# Revit family: EVISA
name_source: partatom
category: Equipement de génie climatique
revit_build: Autodesk Revit 2018 (Build: 20170223_1515(x64)
units: mm (PartAtom-declared; Revit-internal decimal feet)

## family parameters
Basée sur le plan de construction = Non
Classification = Aucun
Cote de connecteur circulaire = Utiliser le diamètre
Couper avec des vides une fois chargée = Non
Partagée = Non
Point de calcul de pièce = Non
Toujours verticalement = Oui
Type d'élément = Normal

## types (13) — shared parameters
BRANCHEMENT_TERRE = Oui
COS_PHI = 0.9
Fabricant = MIL'S
Lien espace client = https://www.mils.fr
Modèle = EVISA
NBR_POLES = 3
TENSION_ALIM = 400 V
ZONE_MAINT_200 = 200 mm
ZONE_MAINT_400 = 400 mm
ØBOUCH_OIL = 48.5 mm
ØVIDANGE = 30 mm  [stored 0.0984252 ft]

## per-type parameters (varying)
- i - E300.R: CHANF.CORPS=50 mm; CHANF.REF.V=40 mm  [stored 0.131234 ft]; CORPS=Oui; DEBIT_ASPI_VIDE=300.0 m³/h; DEBIT_REFOUL_VIDE=300.0 m³/h; DESCR_ALIM_ELECT=Alimentation électrique, 4G2.5mm²; DESCR_ASPI=Aspiration Vide ; 300 m³/h ; G 2" FEM; DESCR_REFOUL=Refoulement Vide ; 300 m³/h ; G 3" FEM; DIAM_ASPI_VIDE=50 mm; DIAM_REFOUL_VIDE=50 mm; HAUTEUR=426 mm; HAUT_BOITE_BORNE=362 mm; HAUT_BOITE_REFOUL.=420 mm; HAUT_BRIDE=360 mm; HAUT_CORPS=312.5 mm; HAUT_FILTRE_HUILE=82.5 mm; HAUT_MOT_ELECT.=170 mm; HAUT_OFFSET_VIDANGE=50 mm; HAUT_REFOUL.=477 mm; HAUT_REFOUL_E25/100.R=67.5 mm; HAUT_SILENTB.=31.5 mm  [stored 0.103346 ft]; LARGEUR=516 mm; LARG_BOITE_BORNE=125 mm; LARG_BOITE_REFOUL.=236 mm; LARG_CORPS=280 mm; LARG_ENTRAXE_SILENTB.=344.5 mm; LARG_OFFSET_BOITE_BORNE=62.5 mm; LARG_OFFSET_BRIDE=141 mm; LARG_OFFSET_CORPS=121 mm; LARG_OFFSET_COUDE_REFOUL.=277 mm; LARG_OFFSET_FILTRE=118 mm; LARG_OFFSET_MOT_ELECT.=35 mm  [stored 0.114829 ft]; LARG_OFFSET_OIL=53 mm; LARG_OFFSET_SILENTB_E25/100.R=235.7 mm; LARG_OFFSET_VIDANGE=192.5 mm; LARG_REFOUL_E25/100.R=62.2 mm; LONGUEUR=1063 mm; LONG_BOITE_BORNE=125 mm; LONG_BOITE_REFOUL.=610 mm; LONG_CORPS=688 mm; LONG_ENTRAXE_SILENTB.=260 mm; LONG_FILTRE_HUILE=138 mm; LONG_MOT_ELECT.=385.5 mm; LONG_OFFSET_BOITE_BORNE=8 mm  [stored 0.0262467 ft]; LONG_OFFSET_BRIDE=306.5 mm; LONG_OFFSET_CORPS=662.5 mm; LONG_OFFSET_REFOUL=440.5 mm; LONG_OFFSET_SILENTB_E25/100.R=104.6 mm; LONG_REFOUL.=61 mm; LONG_ZONE_MAINT=1463 mm; NEUTRE=Non; NIVEAU_SONORE(dB(A))=72; OFFSET_BOITE_REFOUL.=108.5 mm; POIDS(Kg)=172 mm; PROF.VIDANGE=36 mm  [stored 0.11811 ft]; PUISSANCE_APPARENTE=6111 VA; PUISS_ELECT=6 kW; RAY_COUDE_REFOUL.=48 mm; REFOUL_E40-100.R+SILENTB_N°5=Non; SILENTB_N°1=Oui; SILENTB_N°2=Oui; VISIBILITE_BRIDE=Non; ZONE_MAINT_50=161 mm; ØBRIDE=80 mm; ØCOUDE_REFOUL.=60 mm; ØFILTRE_HUILE=100 mm; ØMOT_ELECT.=264 mm; ØSILENTB.=50 mm
- a - E25.2 HV: CHANF.CORPS=36 mm  [stored 0.11811 ft]; CHANF.REF.V=5 mm  [stored 0.0164042 ft]; CORPS=Oui; DEBIT_ASPI_VIDE=30.0 m³/h; DEBIT_REFOUL_VIDE=30.0 m³/h; DESCR_ALIM_ELECT=Alimentation électrique, 4G1.5mm²; DESCR_ASPI=Aspiration Vide ; 30 m³/h ; G 1" FEM; DESCR_REFOUL=Refoulement Vide ; 30 m³/h ; G 1" FEM; DIAM_ASPI_VIDE=25 mm  [stored 0.082021 ft]; DIAM_REFOUL_VIDE=25 mm  [stored 0.082021 ft]; HAUTEUR=276 mm; HAUT_BOITE_BORNE=223 mm; HAUT_BOITE_REFOUL.=265 mm; HAUT_BRIDE=249.5 mm; HAUT_CORPS=209 mm; HAUT_FILTRE_HUILE=59 mm; HAUT_MOT_ELECT.=115.5 mm; HAUT_OFFSET_VIDANGE=29.5 mm; HAUT_REFOUL.=290 mm; HAUT_REFOUL_E25/100.R=67.5 mm; HAUT_SILENTB.=14 mm  [stored 0.0459318 ft]; LARGEUR=296 mm; LARG_BOITE_BORNE=94 mm; LARG_BOITE_REFOUL.=131 mm; LARG_CORPS=165 mm; LARG_ENTRAXE_SILENTB.=189 mm; LARG_OFFSET_BOITE_BORNE=47 mm; LARG_OFFSET_BRIDE=85 mm; LARG_OFFSET_CORPS=92 mm; LARG_OFFSET_COUDE_REFOUL.=144 mm; LARG_OFFSET_FILTRE=75 mm; LARG_OFFSET_MOT_ELECT.=0 mm  [stored 0 ft]; LARG_OFFSET_OIL=44 mm; LARG_OFFSET_SILENTB_E25/100.R=235.7 mm; LARG_OFFSET_VIDANGE=36.5 mm  [stored 0.119751 ft]; LARG_REFOUL_E25/100.R=62.2 mm; LONGUEUR=535 mm; LONG_BOITE_BORNE=94 mm; LONG_BOITE_REFOUL.=370 mm; LONG_CORPS=250 mm; LONG_ENTRAXE_SILENTB.=148 mm; LONG_FILTRE_HUILE=75 mm; LONG_MOT_ELECT.=251 mm; LONG_OFFSET_BOITE_BORNE=37 mm  [stored 0.121391 ft]; LONG_OFFSET_BRIDE=148 mm; LONG_OFFSET_CORPS=235 mm; LONG_OFFSET_REFOUL=174 mm; LONG_OFFSET_SILENTB_E25/100.R=104.6 mm; LONG_REFOUL.=42 mm  [stored 0.137795 ft]; LONG_ZONE_MAINT=935 mm; NEUTRE=Non; NIVEAU_SONORE(dB(A))=60; OFFSET_BOITE_REFOUL.=146 mm; POIDS(Kg)=39 mm  [stored 0.127953 ft]; PROF.VIDANGE=36 mm  [stored 0.11811 ft]; PUISSANCE_APPARENTE=833 VA; PUISS_ELECT=1 kW; RAY_COUDE_REFOUL.=31.2 mm  [stored 0.102362 ft]; REFOUL_E40-100.R+SILENTB_N°5=Non; SILENTB_N°1=Oui; SILENTB_N°2=Oui; VISIBILITE_BRIDE=Non; ZONE_MAINT_50=142 mm; ØBRIDE=50 mm; ØCOUDE_REFOUL.=39 mm  [stored 0.127953 ft]; ØFILTRE_HUILE=76 mm; ØMOT_ELECT.=156 mm; ØSILENTB.=30 mm  [stored 0.0984252 ft]
- j - E350.R: CHANF.CORPS=55 mm; CHANF.REF.V=12 mm  [stored 0.0393701 ft]; CORPS=Oui; DEBIT_ASPI_VIDE=360.0 m³/h; DEBIT_REFOUL_VIDE=360.0 m³/h; DESCR_ALIM_ELECT=Alimentation électrique, 4G4mm²; DESCR_ASPI=Aspiration Vide ; 360 m³/h ; BRIDE DN80; DESCR_REFOUL=Refoulement Vide ; 360 m³/h ; G 3" FEM; DIAM_ASPI_VIDE=80 mm; DIAM_REFOUL_VIDE=80 mm; HAUTEUR=544 mm; HAUT_BOITE_BORNE=443 mm; HAUT_BOITE_REFOUL.=533 mm; HAUT_BRIDE=509 mm; HAUT_CORPS=431 mm; HAUT_FILTRE_HUILE=95 mm; HAUT_MOT_ELECT.=210 mm; HAUT_OFFSET_VIDANGE=46 mm; HAUT_REFOUL.=614 mm; HAUT_REFOUL_E25/100.R=67.5 mm; HAUT_SILENTB.=28 mm  [stored 0.0918635 ft]; LARGEUR=682 mm; LARG_BOITE_BORNE=153 mm; LARG_BOITE_REFOUL.=299 mm; LARG_CORPS=383 mm; LARG_ENTRAXE_SILENTB.=464 mm; LARG_OFFSET_BOITE_BORNE=76.5 mm; LARG_OFFSET_BRIDE=170 mm; LARG_OFFSET_CORPS=188 mm; LARG_OFFSET_COUDE_REFOUL.=349 mm; LARG_OFFSET_FILTRE=220 mm; LARG_OFFSET_MOT_ELECT.=0 mm  [stored 0 ft]; LARG_OFFSET_OIL=51 mm; LARG_OFFSET_SILENTB_E25/100.R=235.7 mm; LARG_OFFSET_VIDANGE=235 mm; LARG_REFOUL_E25/100.R=62.2 mm; LONGUEUR=1360 mm; LONG_BOITE_BORNE=135 mm; LONG_BOITE_REFOUL.=686 mm; LONG_CORPS=837 mm; LONG_ENTRAXE_SILENTB.=376 mm; LONG_FILTRE_HUILE=121 mm; LONG_MOT_ELECT.=510 mm; LONG_OFFSET_BOITE_BORNE=43 mm  [stored 0.141076 ft]; LONG_OFFSET_BRIDE=349 mm; LONG_OFFSET_CORPS=758 mm; LONG_OFFSET_REFOUL=524 mm; LONG_OFFSET_SILENTB_E25/100.R=104.6 mm; LONG_REFOUL.=78 mm; LONG_ZONE_MAINT=1760 mm; NEUTRE=Non; NIVEAU_SONORE(dB(A))=72; OFFSET_BOITE_REFOUL.=82 mm; POIDS(Kg)=363 mm; PROF.VIDANGE=37 mm  [stored 0.121391 ft]; PUISSANCE_APPARENTE=8333 VA; PUISS_ELECT=8 kW; RAY_COUDE_REFOUL.=76 mm; REFOUL_E40-100.R+SILENTB_N°5=Non; SILENTB_N°1=Oui; SILENTB_N°2=Oui; VISIBILITE_BRIDE=Oui; ZONE_MAINT_50=178 mm; ØBRIDE=138 mm; ØCOUDE_REFOUL.=95 mm; ØFILTRE_HUILE=93 mm; ØMOT_ELECT.=310 mm; ØSILENTB.=60 mm
- c - E40.2 HV: CHANF.CORPS=36 mm  [stored 0.11811 ft]; CHANF.REF.V=5 mm  [stored 0.0164042 ft]; CORPS=Oui; DEBIT_ASPI_VIDE=47.7 m³/h; DEBIT_REFOUL_VIDE=47.7 m³/h; DESCR_ALIM_ELECT=Alimentation électrique, 4G1.5mm²; DESCR_ASPI=Aspiration Vide ; 47.7 m³/h ; G 1" FEM; DESCR_REFOUL=Refoulement Vide ; 47.7 m³/h ; G 1" FEM; DIAM_ASPI_VIDE=25 mm  [stored 0.082021 ft]; DIAM_REFOUL_VIDE=25 mm  [stored 0.082021 ft]; HAUTEUR=276 mm; HAUT_BOITE_BORNE=237.5 mm; HAUT_BOITE_REFOUL.=265 mm; HAUT_BRIDE=249.5 mm; HAUT_CORPS=209 mm; HAUT_FILTRE_HUILE=59 mm; HAUT_MOT_ELECT.=111.5 mm; HAUT_OFFSET_VIDANGE=29.5 mm; HAUT_REFOUL.=290 mm; HAUT_REFOUL_E25/100.R=67.5 mm; HAUT_SILENTB.=5 mm  [stored 0.0164042 ft]; LARGEUR=296 mm; LARG_BOITE_BORNE=109.5 mm; LARG_BOITE_REFOUL.=131 mm; LARG_CORPS=165 mm; LARG_ENTRAXE_SILENTB.=189 mm; LARG_OFFSET_BOITE_BORNE=54.8 mm; LARG_OFFSET_BRIDE=85 mm; LARG_OFFSET_CORPS=92 mm; LARG_OFFSET_COUDE_REFOUL.=144 mm; LARG_OFFSET_FILTRE=75 mm; LARG_OFFSET_MOT_ELECT.=0 mm  [stored 0 ft]; LARG_OFFSET_OIL=44 mm; LARG_OFFSET_SILENTB_E25/100.R=235.7 mm; LARG_OFFSET_VIDANGE=36.5 mm  [stored 0.119751 ft]; LARG_REFOUL_E25/100.R=62.2 mm; LONGUEUR=620 mm; LONG_BOITE_BORNE=109.5 mm; LONG_BOITE_REFOUL.=370 mm; LONG_CORPS=345 mm; LONG_ENTRAXE_SILENTB.=185 mm; LONG_FILTRE_HUILE=75 mm; LONG_MOT_ELECT.=274.5 mm; LONG_OFFSET_BOITE_BORNE=27.8 mm  [stored 0.0912073 ft]; LONG_OFFSET_BRIDE=185 mm; LONG_OFFSET_CORPS=337 mm; LONG_OFFSET_REFOUL=211 mm; LONG_OFFSET_SILENTB_E25/100.R=104.6 mm; LONG_REFOUL.=42 mm  [stored 0.137795 ft]; LONG_ZONE_MAINT=1020 mm; NEUTRE=Non; NIVEAU_SONORE(dB(A))=62; OFFSET_BOITE_REFOUL.=109 mm; POIDS(Kg)=52 mm; PROF.VIDANGE=36 mm  [stored 0.11811 ft]; PUISSANCE_APPARENTE=1222 VA; PUISS_ELECT=1 kW; RAY_COUDE_REFOUL.=25.6 mm; REFOUL_E40-100.R+SILENTB_N°5=Non; SILENTB_N°1=Oui; SILENTB_N°2=Oui; VISIBILITE_BRIDE=Non; ZONE_MAINT_50=142 mm; ØBRIDE=50 mm; ØCOUDE_REFOUL.=32 mm  [stored 0.104987 ft]; ØFILTRE_HUILE=76 mm; ØMOT_ELECT.=175 mm; ØSILENTB.=30 mm  [stored 0.0984252 ft]
- g - E150.R: CHANF.CORPS=40 mm  [stored 0.131234 ft]; CHANF.REF.V=40 mm  [stored 0.131234 ft]; CORPS=Oui; DEBIT_ASPI_VIDE=132.0 m³/h; DEBIT_REFOUL_VIDE=132.0 m³/h; DESCR_ALIM_ELECT=Alimentation électrique, 4G2.5mm²; DESCR_ASPI=Aspiration Vide ; 132 m³/h ; G 2" FEM; DESCR_REFOUL=Refoulement Vide ; 132 m³/h ; G 2" FEM; DIAM_ASPI_VIDE=50 mm; DIAM_REFOUL_VIDE=50 mm; HAUTEUR=426 mm; HAUT_BOITE_BORNE=353 mm; HAUT_BOITE_REFOUL.=420 mm; HAUT_BRIDE=360 mm; HAUT_CORPS=312.5 mm; HAUT_FILTRE_HUILE=82.5 mm; HAUT_MOT_ELECT.=168 mm; HAUT_OFFSET_VIDANGE=50 mm; HAUT_REFOUL.=477 mm; HAUT_REFOUL_E25/100.R=67.5 mm; HAUT_SILENTB.=25 mm  [stored 0.082021 ft]; LARGEUR=516 mm; LARG_BOITE_BORNE=127 mm; LARG_BOITE_REFOUL.=238 mm; LARG_CORPS=278 mm; LARG_ENTRAXE_SILENTB.=344.5 mm; LARG_OFFSET_BOITE_BORNE=63.5 mm; LARG_OFFSET_BRIDE=141 mm; LARG_OFFSET_CORPS=121 mm; LARG_OFFSET_COUDE_REFOUL.=277 mm; LARG_OFFSET_FILTRE=118 mm; LARG_OFFSET_MOT_ELECT.=42.5 mm  [stored 0.139436 ft]; LARG_OFFSET_OIL=53 mm; LARG_OFFSET_SILENTB_E25/100.R=235.7 mm; LARG_OFFSET_VIDANGE=192.5 mm; LARG_REFOUL_E25/100.R=62.2 mm; LONGUEUR=919 mm; LONG_BOITE_BORNE=127 mm; LONG_BOITE_REFOUL.=610 mm; LONG_CORPS=504 mm; LONG_ENTRAXE_SILENTB.=260 mm; LONG_FILTRE_HUILE=138 mm; LONG_MOT_ELECT.=385.5 mm; LONG_OFFSET_BOITE_BORNE=33 mm  [stored 0.108268 ft]; LONG_OFFSET_BRIDE=260 mm; LONG_OFFSET_CORPS=478.5 mm; LONG_OFFSET_REFOUL=394 mm; LONG_OFFSET_SILENTB_E25/100.R=104.6 mm; LONG_REFOUL.=65 mm; LONG_ZONE_MAINT=1319 mm; NEUTRE=Non; NIVEAU_SONORE(dB(A))=69; OFFSET_BOITE_REFOUL.=155 mm; POIDS(Kg)=154 mm; PROF.VIDANGE=41 mm  [stored 0.134514 ft]; PUISSANCE_APPARENTE=3333 VA; PUISS_ELECT=3 kW; RAY_COUDE_REFOUL.=51.6 mm; REFOUL_E40-100.R+SILENTB_N°5=Non; SILENTB_N°1=Oui; SILENTB_N°2=Oui; VISIBILITE_BRIDE=Non; ZONE_MAINT_50=165 mm; ØBRIDE=80 mm; ØCOUDE_REFOUL.=64.5 mm; ØFILTRE_HUILE=93 mm; ØMOT_ELECT.=255 mm; ØSILENTB.=50 mm
- h - E200.R: CHANF.CORPS=40 mm  [stored 0.131234 ft]; CHANF.REF.V=40 mm  [stored 0.131234 ft]; CORPS=Oui; DEBIT_ASPI_VIDE=200.0 m³/h; DEBIT_REFOUL_VIDE=200.0 m³/h; DESCR_ALIM_ELECT=Alimentation électrique, 4G2.5mm²; DESCR_ASPI=Aspiration Vide ; 200 m³/h ; G 2" FEM; DESCR_REFOUL=Refoulement Vide ; 200 m³/h ; G 2" FEM; DIAM_ASPI_VIDE=50 mm; DIAM_REFOUL_VIDE=50 mm; HAUTEUR=426 mm; HAUT_BOITE_BORNE=320 mm; HAUT_BOITE_REFOUL.=420 mm; HAUT_BRIDE=360 mm; HAUT_CORPS=312.5 mm; HAUT_FILTRE_HUILE=82.5 mm; HAUT_MOT_ELECT.=172 mm; HAUT_OFFSET_VIDANGE=50 mm; HAUT_REFOUL.=477 mm; HAUT_REFOUL_E25/100.R=67.5 mm; HAUT_SILENTB.=25 mm  [stored 0.082021 ft]; LARGEUR=516 mm; LARG_BOITE_BORNE=86 mm; LARG_BOITE_REFOUL.=238 mm; LARG_CORPS=278 mm; LARG_ENTRAXE_SILENTB.=344.5 mm; LARG_OFFSET_BOITE_BORNE=43 mm  [stored 0.141076 ft]; LARG_OFFSET_BRIDE=141 mm; LARG_OFFSET_CORPS=121 mm; LARG_OFFSET_COUDE_REFOUL.=277 mm; LARG_OFFSET_FILTRE=118 mm; LARG_OFFSET_MOT_ELECT.=35 mm  [stored 0.114829 ft]; LARG_OFFSET_OIL=53 mm; LARG_OFFSET_SILENTB_E25/100.R=235.7 mm; LARG_OFFSET_VIDANGE=192.5 mm; LARG_REFOUL_E25/100.R=62.2 mm; LONGUEUR=917 mm; LONG_BOITE_BORNE=86 mm; LONG_BOITE_REFOUL.=610 mm; LONG_CORPS=594.5 mm; LONG_ENTRAXE_SILENTB.=260 mm; LONG_FILTRE_HUILE=138 mm; LONG_MOT_ELECT.=323 mm; LONG_OFFSET_BOITE_BORNE=31.7 mm  [stored 0.104003 ft]; LONG_OFFSET_BRIDE=260 mm; LONG_OFFSET_CORPS=569 mm; LONG_OFFSET_REFOUL=394 mm; LONG_OFFSET_SILENTB_E25/100.R=104.6 mm; LONG_REFOUL.=61 mm; LONG_ZONE_MAINT=1317 mm; NEUTRE=Non; NIVEAU_SONORE(dB(A))=71; OFFSET_BOITE_REFOUL.=155 mm; POIDS(Kg)=143 mm; PROF.VIDANGE=38 mm  [stored 0.124672 ft]; PUISSANCE_APPARENTE=4444 VA; PUISS_ELECT=4 kW; RAY_COUDE_REFOUL.=51.6 mm; REFOUL_E40-100.R+SILENTB_N°5=Non; SILENTB_N°1=Oui; SILENTB_N°2=Oui; VISIBILITE_BRIDE=Non; ZONE_MAINT_50=161 mm; ØBRIDE=80 mm; ØCOUDE_REFOUL.=64.5 mm; ØFILTRE_HUILE=93 mm; ØMOT_ELECT.=220 mm; ØSILENTB.=50 mm
- k - E400.R: CHANF.CORPS=55 mm; CHANF.REF.V=10 mm  [stored 0.0328084 ft]; CORPS=Oui; DEBIT_ASPI_VIDE=426.0 m³/h; DEBIT_REFOUL_VIDE=426.0 m³/h; DESCR_ALIM_ELECT=Alimentation électrique, 4G6mm²; DESCR_ASPI=Aspiration Vide ; 426 m³/h ; BRIDE DN80; DESCR_REFOUL=Refoulement Vide ; 426 m³/h ; G 3" FEM; DIAM_ASPI_VIDE=80 mm; DIAM_REFOUL_VIDE=80 mm; HAUTEUR=544 mm; HAUT_BOITE_BORNE=443 mm; HAUT_BOITE_REFOUL.=533 mm; HAUT_BRIDE=509 mm; HAUT_CORPS=431 mm; HAUT_FILTRE_HUILE=95 mm; HAUT_MOT_ELECT.=210 mm; HAUT_OFFSET_VIDANGE=46 mm; HAUT_REFOUL.=614 mm; HAUT_REFOUL_E25/100.R=67.5 mm; HAUT_SILENTB.=28 mm  [stored 0.0918635 ft]; LARGEUR=680 mm; LARG_BOITE_BORNE=153 mm; LARG_BOITE_REFOUL.=299 mm; LARG_CORPS=383 mm; LARG_ENTRAXE_SILENTB.=464 mm; LARG_OFFSET_BOITE_BORNE=76.5 mm; LARG_OFFSET_BRIDE=170 mm; LARG_OFFSET_CORPS=188 mm; LARG_OFFSET_COUDE_REFOUL.=349 mm; LARG_OFFSET_FILTRE=220 mm; LARG_OFFSET_MOT_ELECT.=0 mm  [stored 0 ft]; LARG_OFFSET_OIL=51 mm; LARG_OFFSET_SILENTB_E25/100.R=235.7 mm; LARG_OFFSET_VIDANGE=235 mm; LARG_REFOUL_E25/100.R=62.2 mm; LONGUEUR=1400 mm; LONG_BOITE_BORNE=135 mm; LONG_BOITE_REFOUL.=685.5 mm; LONG_CORPS=883.5 mm; LONG_ENTRAXE_SILENTB.=376 mm; LONG_FILTRE_HUILE=121 mm; LONG_MOT_ELECT.=510 mm; LONG_OFFSET_BOITE_BORNE=43 mm  [stored 0.141076 ft]; LONG_OFFSET_BRIDE=376 mm; LONG_OFFSET_CORPS=827.5 mm; LONG_OFFSET_REFOUL=523.5 mm; LONG_OFFSET_SILENTB_E25/100.R=104.6 mm; LONG_REFOUL.=78 mm; LONG_ZONE_MAINT=1800 mm; NEUTRE=Non; NIVEAU_SONORE(dB(A))=72; OFFSET_BOITE_REFOUL.=81.5 mm; POIDS(Kg)=408 mm; PROF.VIDANGE=27.5 mm  [stored 0.0902231 ft]; PUISSANCE_APPARENTE=10000 VA; PUISS_ELECT=9 kW; RAY_COUDE_REFOUL.=76 mm; REFOUL_E40-100.R+SILENTB_N°5=Non; SILENTB_N°1=Oui; SILENTB_N°2=Oui; VISIBILITE_BRIDE=Oui; ZONE_MAINT_50=178 mm; ØBRIDE=138 mm; ØCOUDE_REFOUL.=95 mm; ØFILTRE_HUILE=93 mm; ØMOT_ELECT.=310 mm; ØSILENTB.=60 mm
- l - E500.R: CHANF.CORPS=55 mm; CHANF.REF.V=12 mm  [stored 0.0393701 ft]; CORPS=Oui; DEBIT_ASPI_VIDE=513.0 m³/h; DEBIT_REFOUL_VIDE=513.0 m³/h; DESCR_ALIM_ELECT=Alimentation électrique, 4G6mm²; DESCR_ASPI=Aspiration Vide ; 513 m³/h ; BRIDE DN80; DESCR_REFOUL=Refoulement Vide ; 513 m³/h ; G 3" FEM; DIAM_ASPI_VIDE=80 mm; DIAM_REFOUL_VIDE=80 mm; HAUTEUR=544 mm; HAUT_BOITE_BORNE=466 mm; HAUT_BOITE_REFOUL.=533 mm; HAUT_BRIDE=509 mm; HAUT_CORPS=431 mm; HAUT_FILTRE_HUILE=95 mm; HAUT_MOT_ELECT.=210 mm; HAUT_OFFSET_VIDANGE=46 mm; HAUT_REFOUL.=614 mm; HAUT_REFOUL_E25/100.R=67.5 mm; HAUT_SILENTB.=28 mm  [stored 0.0918635 ft]; LARGEUR=680 mm; LARG_BOITE_BORNE=210 mm; LARG_BOITE_REFOUL.=299 mm; LARG_CORPS=381 mm; LARG_ENTRAXE_SILENTB.=464 mm; LARG_OFFSET_BOITE_BORNE=105 mm; LARG_OFFSET_BRIDE=168 mm; LARG_OFFSET_CORPS=186 mm; LARG_OFFSET_COUDE_REFOUL.=349 mm; LARG_OFFSET_FILTRE=220 mm; LARG_OFFSET_MOT_ELECT.=0 mm  [stored 0 ft]; LARG_OFFSET_OIL=51 mm; LARG_OFFSET_SILENTB_E25/100.R=235.7 mm; LARG_OFFSET_VIDANGE=235 mm; LARG_REFOUL_E25/100.R=62.2 mm; LONGUEUR=1500 mm; LONG_BOITE_BORNE=180 mm; LONG_BOITE_REFOUL.=685.5 mm; LONG_CORPS=943.5 mm; LONG_ENTRAXE_SILENTB.=376 mm; LONG_FILTRE_HUILE=121 mm; LONG_MOT_ELECT.=552 mm; LONG_OFFSET_BOITE_BORNE=67 mm; LONG_OFFSET_BRIDE=376 mm; LONG_OFFSET_CORPS=853.5 mm; LONG_OFFSET_REFOUL=523.5 mm; LONG_OFFSET_SILENTB_E25/100.R=104.6 mm; LONG_REFOUL.=78 mm; LONG_ZONE_MAINT=1900 mm; NEUTRE=Non; NIVEAU_SONORE(dB(A))=73; OFFSET_BOITE_REFOUL.=81.5 mm; POIDS(Kg)=462 mm; PROF.VIDANGE=27.5 mm  [stored 0.0902231 ft]; PUISSANCE_APPARENTE=12222 VA; PUISS_ELECT=11 kW; RAY_COUDE_REFOUL.=76 mm; REFOUL_E40-100.R+SILENTB_N°5=Non; SILENTB_N°1=Oui; SILENTB_N°2=Oui; VISIBILITE_BRIDE=Oui; ZONE_MAINT_50=178 mm; ØBRIDE=138 mm; ØCOUDE_REFOUL.=95 mm; ØFILTRE_HUILE=93 mm; ØMOT_ELECT.=348 mm; ØSILENTB.=60 mm
- m - E600.R: CHANF.CORPS=55 mm; CHANF.REF.V=12 mm  [stored 0.0393701 ft]; CORPS=Oui; DEBIT_ASPI_VIDE=635.0 m³/h; DEBIT_REFOUL_VIDE=635.0 m³/h; DESCR_ALIM_ELECT=Alimentation électrique 4G10mm²; DESCR_ASPI=Aspiration Vide ; 635 m³/h ; BRIDE DN80; DESCR_REFOUL=Refoulement Vide ; 635 m³/h ; G 3" FEM; DIAM_ASPI_VIDE=80 mm; DIAM_REFOUL_VIDE=80 mm; HAUTEUR=544 mm; HAUT_BOITE_BORNE=466 mm; HAUT_BOITE_REFOUL.=533 mm; HAUT_BRIDE=509 mm; HAUT_CORPS=431 mm; HAUT_FILTRE_HUILE=95 mm; HAUT_MOT_ELECT.=210 mm; HAUT_OFFSET_VIDANGE=46 mm; HAUT_REFOUL.=611 mm; HAUT_REFOUL_E25/100.R=67.5 mm; HAUT_SILENTB.=28 mm  [stored 0.0918635 ft]; LARGEUR=680 mm; LARG_BOITE_BORNE=210 mm; LARG_BOITE_REFOUL.=299 mm; LARG_CORPS=381 mm; LARG_ENTRAXE_SILENTB.=464 mm; LARG_OFFSET_BOITE_BORNE=105 mm; LARG_OFFSET_BRIDE=168 mm; LARG_OFFSET_CORPS=186 mm; LARG_OFFSET_COUDE_REFOUL.=349 mm; LARG_OFFSET_FILTRE=220 mm; LARG_OFFSET_MOT_ELECT.=0 mm  [stored 0 ft]; LARG_OFFSET_OIL=51 mm; LARG_OFFSET_SILENTB_E25/100.R=235.7 mm; LARG_OFFSET_VIDANGE=235 mm; LARG_REFOUL_E25/100.R=62.2 mm; LONGUEUR=1655 mm; LONG_BOITE_BORNE=180 mm; LONG_BOITE_REFOUL.=685.5 mm; LONG_CORPS=1035 mm; LONG_ENTRAXE_SILENTB.=376 mm; LONG_FILTRE_HUILE=121 mm; LONG_MOT_ELECT.=614 mm; LONG_OFFSET_BOITE_BORNE=65.5 mm; LONG_OFFSET_BRIDE=376 mm; LONG_OFFSET_CORPS=900 mm; LONG_OFFSET_REFOUL=523.5 mm; LONG_OFFSET_SILENTB_E25/100.R=104.6 mm; LONG_REFOUL.=78 mm; LONG_ZONE_MAINT=2055 mm; NEUTRE=Non; NIVEAU_SONORE(dB(A))=74; OFFSET_BOITE_REFOUL.=81.5 mm; POIDS(Kg)=531 mm; PROF.VIDANGE=27.5 mm  [stored 0.0902231 ft]; PUISSANCE_APPARENTE=14444 VA; PUISS_ELECT=13 kW; RAY_COUDE_REFOUL.=76 mm; REFOUL_E40-100.R+SILENTB_N°5=Non; SILENTB_N°1=Oui; SILENTB_N°2=Oui; VISIBILITE_BRIDE=Oui; ZONE_MAINT_50=178 mm; ØBRIDE=138 mm; ØCOUDE_REFOUL.=95 mm; ØFILTRE_HUILE=93 mm; ØMOT_ELECT.=348 mm; ØSILENTB.=60 mm
- b - E25.R: CHANF.CORPS=36 mm  [stored 0.11811 ft]; CHANF.REF.V=5 mm  [stored 0.0164042 ft]; CORPS=Non; DEBIT_ASPI_VIDE=28.0 m³/h; DEBIT_REFOUL_VIDE=28.0 m³/h; DESCR_ALIM_ELECT=Alimentation électrique, 4G1.5mm²; DESCR_ASPI=Aspiration Vide ; 28 m³/h ; G 1" FEM; DESCR_REFOUL=Refoulement Vide ; 28 m³/h ; G 1" FEM; DIAM_ASPI_VIDE=25 mm  [stored 0.082021 ft]; DIAM_REFOUL_VIDE=25 mm  [stored 0.082021 ft]; HAUTEUR=258 mm; HAUT_BOITE_BORNE=237 mm; HAUT_BOITE_REFOUL.=258 mm; HAUT_BRIDE=228 mm; HAUT_CORPS=180 mm; HAUT_FILTRE_HUILE=65.5 mm; HAUT_MOT_ELECT.=115.5 mm; HAUT_OFFSET_VIDANGE=38.5 mm  [stored 0.126312 ft]; HAUT_REFOUL.=225 mm; HAUT_REFOUL_E25/100.R=55 mm; HAUT_SILENTB.=21 mm  [stored 0.0688976 ft]; LARGEUR=300 mm; LARG_BOITE_BORNE=85 mm; LARG_BOITE_REFOUL.=128 mm; LARG_CORPS=172.2 mm; LARG_ENTRAXE_SILENTB.=253.5 mm; LARG_OFFSET_BOITE_BORNE=42.5 mm  [stored 0.139436 ft]; LARG_OFFSET_BRIDE=85 mm; LARG_OFFSET_CORPS=22.2 mm  [stored 0.0728346 ft]; LARG_OFFSET_COUDE_REFOUL.=131 mm; LARG_OFFSET_FILTRE=62 mm; LARG_OFFSET_MOT_ELECT.=72.3 mm; LARG_OFFSET_OIL=44 mm; LARG_OFFSET_SILENTB_E25/100.R=253.5 mm; LARG_OFFSET_VIDANGE=63.3 mm; LARG_REFOUL_E25/100.R=45 mm; LONGUEUR=443 mm; LONG_BOITE_BORNE=85 mm; LONG_BOITE_REFOUL.=312 mm; LONG_CORPS=49 mm; LONG_ENTRAXE_SILENTB.=187 mm; LONG_FILTRE_HUILE=76 mm; LONG_MOT_ELECT.=397.5 mm; LONG_OFFSET_BOITE_BORNE=179 mm; LONG_OFFSET_BRIDE=159 mm; LONG_OFFSET_CORPS=300 mm; LONG_OFFSET_REFOUL=214 mm; LONG_OFFSET_SILENTB_E25/100.R=104.6 mm; LONG_REFOUL.=31 mm; LONG_ZONE_MAINT=843 mm; NEUTRE=Oui; NIVEAU_SONORE(dB(A))=59; OFFSET_BOITE_REFOUL.=67 mm; POIDS(Kg)=30 mm  [stored 0.0984252 ft]; PROF.VIDANGE=37 mm  [stored 0.121391 ft]; PUISSANCE_APPARENTE=833 VA; PUISS_ELECT=1 kW; RAY_COUDE_REFOUL.=24 mm  [stored 0.0787402 ft]; REFOUL_E40-100.R+SILENTB_N°5=Oui; SILENTB_N°1=Non; SILENTB_N°2=Non; VISIBILITE_BRIDE=Non; ZONE_MAINT_50=131 mm; ØBRIDE=50 mm; ØCOUDE_REFOUL.=30 mm  [stored 0.0984252 ft]; ØFILTRE_HUILE=76 mm; ØMOT_ELECT.=189 mm; ØSILENTB.=30 mm  [stored 0.0984252 ft]
- d - E40.R: CHANF.CORPS=36 mm  [stored 0.11811 ft]; CHANF.REF.V=5 mm  [stored 0.0164042 ft]; CORPS=Non; DEBIT_ASPI_VIDE=44.0 m³/h; DEBIT_REFOUL_VIDE=44.0 m³/h; DESCR_ALIM_ELECT=Alimentation électrique, 4G1.5mm²; DESCR_ASPI=Aspiration Vide ; 44 m³/h ; G 1" FEM; DESCR_REFOUL=Refoulement Vide ; 44 m³/h ; G 1" FEM; DIAM_ASPI_VIDE=25 mm  [stored 0.082021 ft]; DIAM_REFOUL_VIDE=25 mm  [stored 0.082021 ft]; HAUTEUR=258 mm; HAUT_BOITE_BORNE=237 mm; HAUT_BOITE_REFOUL.=257 mm; HAUT_BRIDE=228 mm; HAUT_CORPS=180 mm; HAUT_FILTRE_HUILE=65.5 mm; HAUT_MOT_ELECT.=115.5 mm; HAUT_OFFSET_VIDANGE=38.5 mm  [stored 0.126312 ft]; HAUT_REFOUL.=225 mm; HAUT_REFOUL_E25/100.R=55 mm; HAUT_SILENTB.=21 mm  [stored 0.0688976 ft]; LARGEUR=300 mm; LARG_BOITE_BORNE=85 mm; LARG_BOITE_REFOUL.=128 mm; LARG_CORPS=172.2 mm; LARG_ENTRAXE_SILENTB.=253.5 mm; LARG_OFFSET_BOITE_BORNE=42.5 mm  [stored 0.139436 ft]; LARG_OFFSET_BRIDE=85 mm; LARG_OFFSET_CORPS=22.2 mm  [stored 0.0728346 ft]; LARG_OFFSET_COUDE_REFOUL.=131 mm; LARG_OFFSET_FILTRE=62 mm; LARG_OFFSET_MOT_ELECT.=72.3 mm; LARG_OFFSET_OIL=44 mm; LARG_OFFSET_SILENTB_E25/100.R=253.5 mm; LARG_OFFSET_VIDANGE=63.3 mm; LARG_REFOUL_E25/100.R=47.5 mm; LONGUEUR=443 mm; LONG_BOITE_BORNE=85 mm; LONG_BOITE_REFOUL.=312 mm; LONG_CORPS=49 mm; LONG_ENTRAXE_SILENTB.=187 mm; LONG_FILTRE_HUILE=76 mm; LONG_MOT_ELECT.=397.5 mm; LONG_OFFSET_BOITE_BORNE=179 mm; LONG_OFFSET_BRIDE=159 mm; LONG_OFFSET_CORPS=300 mm; LONG_OFFSET_REFOUL=214 mm; LONG_OFFSET_SILENTB_E25/100.R=104.6 mm; LONG_REFOUL.=31 mm; LONG_ZONE_MAINT=843 mm; NEUTRE=Non; NIVEAU_SONORE(dB(A))=58; OFFSET_BOITE_REFOUL.=67 mm; POIDS(Kg)=34.3 mm  [stored 0.112533 ft]; PROF.VIDANGE=37 mm  [stored 0.121391 ft]; PUISSANCE_APPARENTE=1222 VA; PUISS_ELECT=1 kW; RAY_COUDE_REFOUL.=24 mm  [stored 0.0787402 ft]; REFOUL_E40-100.R+SILENTB_N°5=Oui; SILENTB_N°1=Non; SILENTB_N°2=Non; VISIBILITE_BRIDE=Non; ZONE_MAINT_50=131 mm; ØBRIDE=50 mm; ØCOUDE_REFOUL.=30 mm  [stored 0.0984252 ft]; ØFILTRE_HUILE=76 mm; ØMOT_ELECT.=189 mm; ØSILENTB.=30 mm  [stored 0.0984252 ft]
- e - E65.R: CHANF.CORPS=36 mm  [stored 0.11811 ft]; CHANF.REF.V=25 mm  [stored 0.082021 ft]; CORPS=Non; DEBIT_ASPI_VIDE=68.0 m³/h; DEBIT_REFOUL_VIDE=68.0 m³/h; DESCR_ALIM_ELECT=Alimentation électrique, 4G1.5mm²; DESCR_ASPI=Aspiration Vide ; 68 m³/h ; G 1"1/4 FEM; DESCR_REFOUL=Refoulement Vide ; 68 m³/h ; G 1"1/4 FEM; DIAM_ASPI_VIDE=32 mm  [stored 0.104987 ft]; DIAM_REFOUL_VIDE=32 mm  [stored 0.104987 ft]; HAUTEUR=285 mm; HAUT_BOITE_BORNE=253 mm; HAUT_BOITE_REFOUL.=285 mm; HAUT_BRIDE=279 mm; HAUT_CORPS=180 mm; HAUT_FILTRE_HUILE=65.5 mm; HAUT_MOT_ELECT.=127 mm; HAUT_OFFSET_VIDANGE=43.5 mm  [stored 0.142717 ft]; HAUT_REFOUL.=248 mm; HAUT_REFOUL_E25/100.R=60 mm; HAUT_SILENTB.=23 mm  [stored 0.0754593 ft]; LARGEUR=331 mm; LARG_BOITE_BORNE=110 mm; LARG_BOITE_REFOUL.=127 mm; LARG_CORPS=204 mm; LARG_ENTRAXE_SILENTB.=205 mm; LARG_OFFSET_BOITE_BORNE=55 mm; LARG_OFFSET_BRIDE=107.5 mm; LARG_OFFSET_CORPS=99 mm; LARG_OFFSET_COUDE_REFOUL.=78.5 mm; LARG_OFFSET_FILTRE=62 mm; LARG_OFFSET_MOT_ELECT.=8.5 mm  [stored 0.0278871 ft]; LARG_OFFSET_OIL=55.5 mm; LARG_OFFSET_SILENTB_E25/100.R=234 mm; LARG_OFFSET_VIDANGE=63.5 mm; LARG_REFOUL_E25/100.R=48.5 mm; LONGUEUR=697 mm; LONG_BOITE_BORNE=110 mm; LONG_BOITE_REFOUL.=567.5 mm; LONG_CORPS=49 mm; LONG_ENTRAXE_SILENTB.=351 mm; LONG_FILTRE_HUILE=76 mm; LONG_MOT_ELECT.=686 mm; LONG_OFFSET_BOITE_BORNE=411 mm; LONG_OFFSET_BRIDE=351 mm; LONG_OFFSET_CORPS=571 mm; LONG_OFFSET_REFOUL=449.5 mm; LONG_OFFSET_SILENTB_E25/100.R=200.5 mm; LONG_REFOUL.=20 mm  [stored 0.0656168 ft]; LONG_ZONE_MAINT=1097 mm; NEUTRE=Non; NIVEAU_SONORE(dB(A))=67; OFFSET_BOITE_REFOUL.=98 mm; POIDS(Kg)=63.4 mm; PROF.VIDANGE=51.3 mm; PUISSANCE_APPARENTE=1667 VA; PUISS_ELECT=2 kW; RAY_COUDE_REFOUL.=12 mm  [stored 0.0393701 ft]; REFOUL_E40-100.R+SILENTB_N°5=Oui; SILENTB_N°1=Non; SILENTB_N°2=Oui; VISIBILITE_BRIDE=Non; ZONE_MAINT_50=120 mm; ØBRIDE=60 mm; ØCOUDE_REFOUL.=15 mm  [stored 0.0492126 ft]; ØFILTRE_HUILE=76 mm; ØMOT_ELECT.=215 mm; ØSILENTB.=30 mm  [stored 0.0984252 ft]
- f - E100.R: CHANF.CORPS=36 mm  [stored 0.11811 ft]; CHANF.REF.V=25 mm  [stored 0.082021 ft]; CORPS=Non; DEBIT_ASPI_VIDE=100.0 m³/h; DEBIT_REFOUL_VIDE=100.0 m³/h; DESCR_ALIM_ELECT=Alimentation électrique, 4G1.5mm²; DESCR_ASPI=Aspiration Vide ; 100 m³/h ; G 1"1/4 FEM; DESCR_REFOUL=Refoulement Vide ; 100 m³/h ; G 1"1/4 FEM; DIAM_ASPI_VIDE=32 mm  [stored 0.104987 ft]; DIAM_REFOUL_VIDE=32 mm  [stored 0.104987 ft]; HAUTEUR=285 mm; HAUT_BOITE_BORNE=253 mm; HAUT_BOITE_REFOUL.=285 mm; HAUT_BRIDE=279 mm; HAUT_CORPS=180 mm; HAUT_FILTRE_HUILE=65.5 mm; HAUT_MOT_ELECT.=127 mm; HAUT_OFFSET_VIDANGE=43.5 mm  [stored 0.142717 ft]; HAUT_REFOUL.=248 mm; HAUT_REFOUL_E25/100.R=60 mm; HAUT_SILENTB.=23 mm  [stored 0.0754593 ft]; LARGEUR=331 mm; LARG_BOITE_BORNE=110 mm; LARG_BOITE_REFOUL.=124 mm; LARG_CORPS=207 mm; LARG_ENTRAXE_SILENTB.=205 mm; LARG_OFFSET_BOITE_BORNE=55 mm; LARG_OFFSET_BRIDE=97 mm; LARG_OFFSET_CORPS=99 mm; LARG_OFFSET_COUDE_REFOUL.=79.5 mm; LARG_OFFSET_FILTRE=62 mm; LARG_OFFSET_MOT_ELECT.=8.5 mm  [stored 0.0278871 ft]; LARG_OFFSET_OIL=55.5 mm; LARG_OFFSET_SILENTB_E25/100.R=235.8 mm; LARG_OFFSET_VIDANGE=63.5 mm; LARG_REFOUL_E25/100.R=50 mm; LONGUEUR=697 mm; LONG_BOITE_BORNE=110 mm; LONG_BOITE_REFOUL.=567.5 mm; LONG_CORPS=49 mm; LONG_ENTRAXE_SILENTB.=351 mm; LONG_FILTRE_HUILE=76 mm; LONG_MOT_ELECT.=686 mm; LONG_OFFSET_BOITE_BORNE=411 mm; LONG_OFFSET_BRIDE=351 mm; LONG_OFFSET_CORPS=571 mm; LONG_OFFSET_REFOUL=498 mm; LONG_OFFSET_SILENTB_E25/100.R=200.5 mm; LONG_REFOUL.=20 mm  [stored 0.0656168 ft]; LONG_ZONE_MAINT=1097 mm; NEUTRE=Non; NIVEAU_SONORE(dB(A))=67; OFFSET_BOITE_REFOUL.=49.2 mm; POIDS(Kg)=67.2 mm; PROF.VIDANGE=51.3 mm; PUISSANCE_APPARENTE=2444 VA; PUISS_ELECT=2 kW; RAY_COUDE_REFOUL.=12 mm  [stored 0.0393701 ft]; REFOUL_E40-100.R+SILENTB_N°5=Oui; SILENTB_N°1=Non; SILENTB_N°2=Oui; VISIBILITE_BRIDE=Non; ZONE_MAINT_50=120 mm; ØBRIDE=60 mm; ØCOUDE_REFOUL.=15 mm  [stored 0.0492126 ft]; ØFILTRE_HUILE=76 mm; ØMOT_ELECT.=215 mm; ØSILENTB.=30 mm  [stored 0.0984252 ft]

note: [stored X ft] marks values corroborated as IEEE doubles in the binary element streams (Revit-internal decimal feet)
